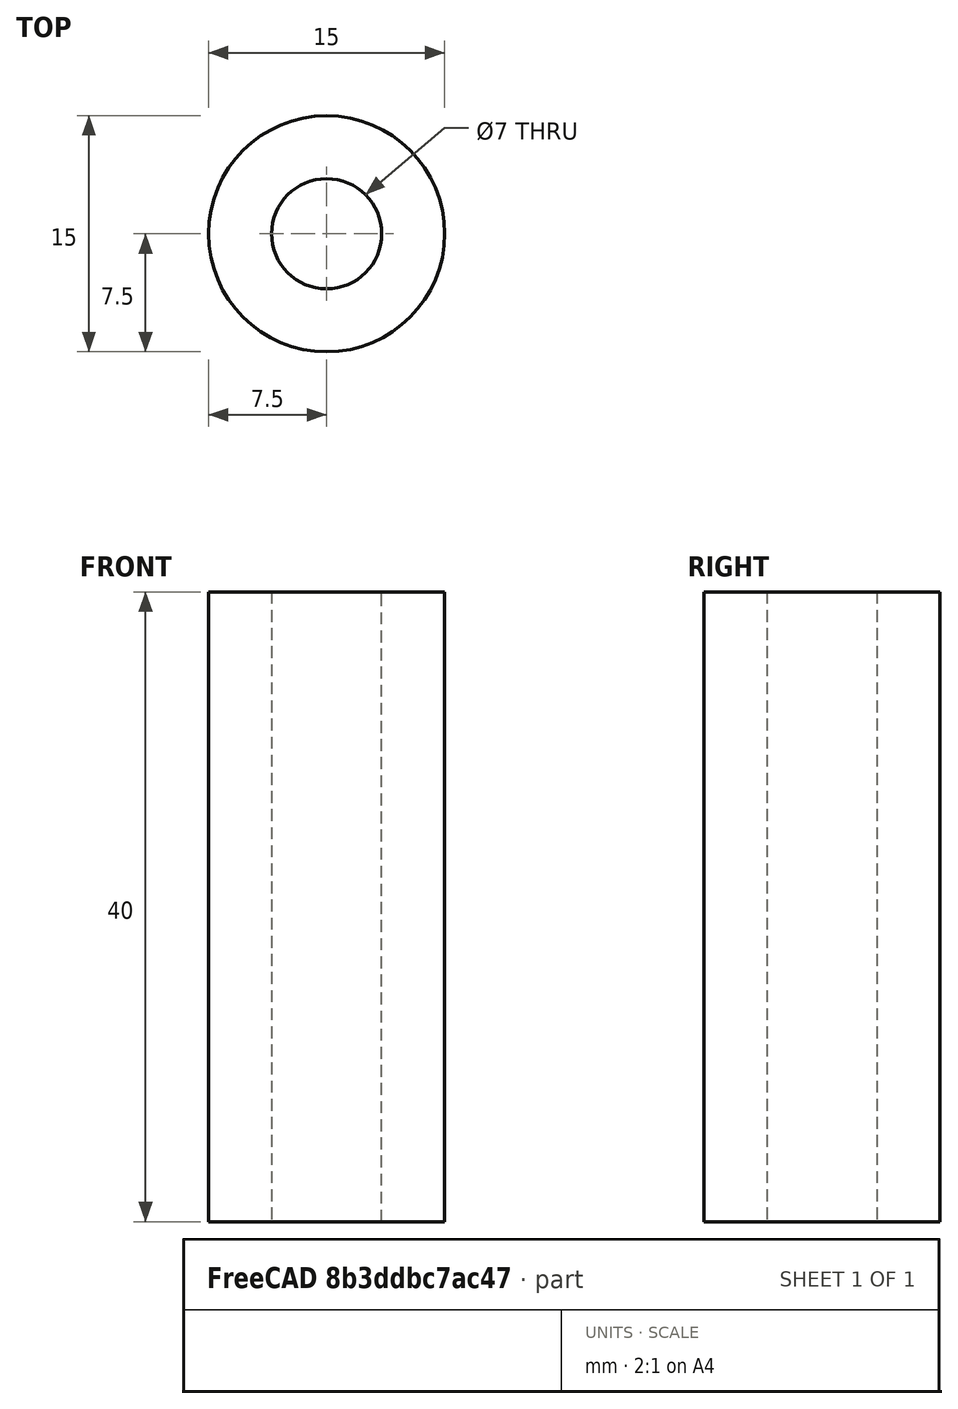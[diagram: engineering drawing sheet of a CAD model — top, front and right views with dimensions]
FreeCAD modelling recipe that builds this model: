
FCSTD DOCUMENT  (FreeCAD 0.19R24276 (Git))
Label: kran_holder_part1
License: All rights reserved
LicenseURL: http://en.wikipedia.org/wiki/All_rights_reserved
objects: Sketcher::SketchObject×2, PartDesign::Pad×1, PartDesign::Body×1
note: 5 computed .brp shape members not serialized (recipe doc carries the construction recipe); baked Part::Feature solids carry a one-line shape summary decoded from their .brp

FEATURE [Sketcher::SketchObject] Sketch
  FullyConstrained = true
  MapMode = 5
  Support = -> [XY_Plane]
  sketch-geometry (2):
    g0: Circle CenterX=0 CenterY=0 CenterZ=0 NormalX=0 NormalY=0 NormalZ=1 AngleXU=0 Radius=3.5
    g1: Circle CenterX=0 CenterY=0 CenterZ=0 NormalX=0 NormalY=0 NormalZ=1 AngleXU=0 Radius=7.5
  constraints (4):
    c: Coincident(g0,g-1)
    c: Diameter(g0) = 7
    c: Coincident(g1,g-1)
    c: Diameter(g1) = 15
FEATURE [PartDesign::Pad] Pad
  Direction = (1,1,1)
  Length = 40
  Length2 = 100
  Profile = -> Sketch
  Type = 0
FEATURE [Sketcher::SketchObject] Sketch001
  FullyConstrained = true
  MapMode = 5
  Placement = pos=(0,0,0) rot=(1,0,0;1.5708rad)
  Support = -> [XZ_Plane]
FEATURE [PartDesign::Body] Body
  Group = -> [Sketch,Pad,Sketch001]
  Origin = -> Origin
  Tip = -> Pad
